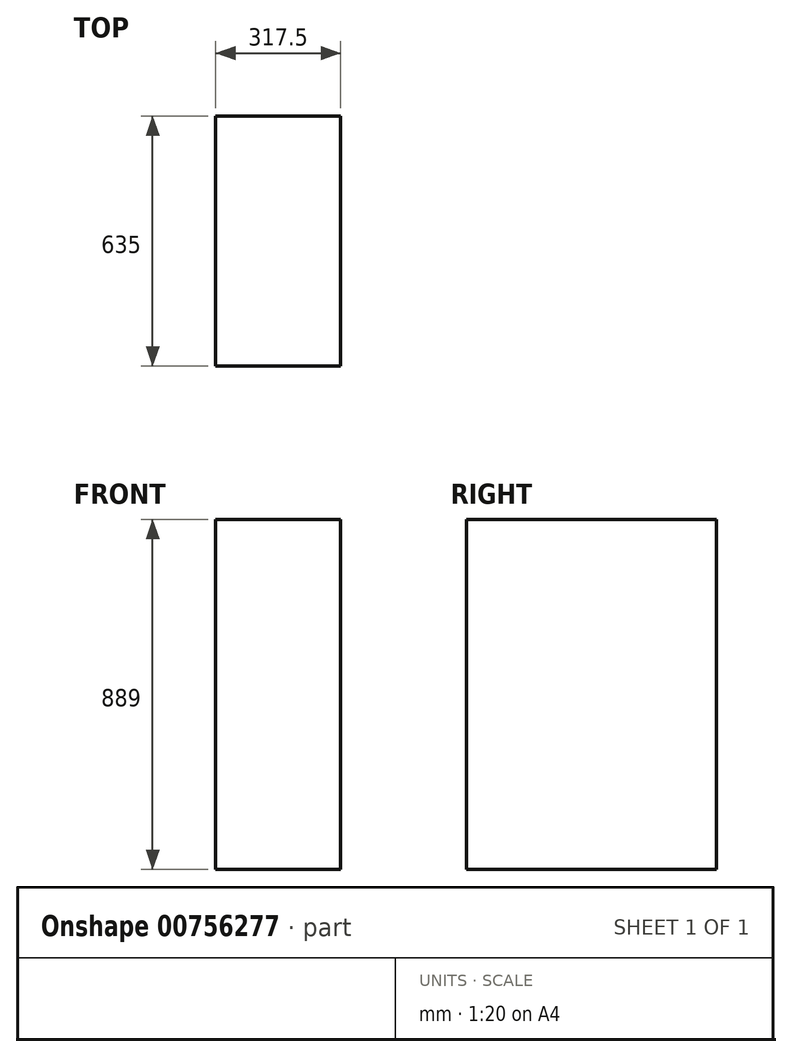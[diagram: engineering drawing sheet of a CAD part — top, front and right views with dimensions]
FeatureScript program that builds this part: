
annotation { "Feature Type Name" : "Feature", "Feature Type Description" : "" }
export const myFeature = defineFeature(function(context is Context, id is Id, definition is map)
    precondition{}
    {
        {
            var Q0;
            Q0=qCreatedBy(makeId("Front.planeOp"),FACE);
            var sketch = newSketch(context, id + "F0", { "sketchPlane" : qUnion([Q0])});
            skLineSegment(sketch, "E0.bottom", {"start": v(0, 0) * mm, "end": v(317.5, 0) * mm});
            skLineSegment(sketch, "E0.top", {"start": v(0, 889) * mm, "end": v(317.5, 889) * mm});
            skLineSegment(sketch, "E0.left", {"start": v(0, 0) * mm, "end": v(0, 889) * mm});
            skLineSegment(sketch, "E0.right", {"start": v(317.5, 0) * mm, "end": v(317.5, 889) * mm});
            skSolve(sketch);
        }
        {
            var Q0;
            Q0=makeQuery(id+"F0.imprint","IMPRINT",FACE,{"disambiguationData":[TD([[makeQuery(id+"F0.imprint","IMPRINT",EDGE,{"derivedFrom":sQuery(id+"F0.wireOp",EDGE,"E0.bottom")}),1.0]])]});
            extrude(context, id + "F1", {"entities" : qUnion([Q0]), "oppositeDirection" : true, "depth" : 635 * mm, "offsetDistance" : 25.4 * mm});
        }
    });
